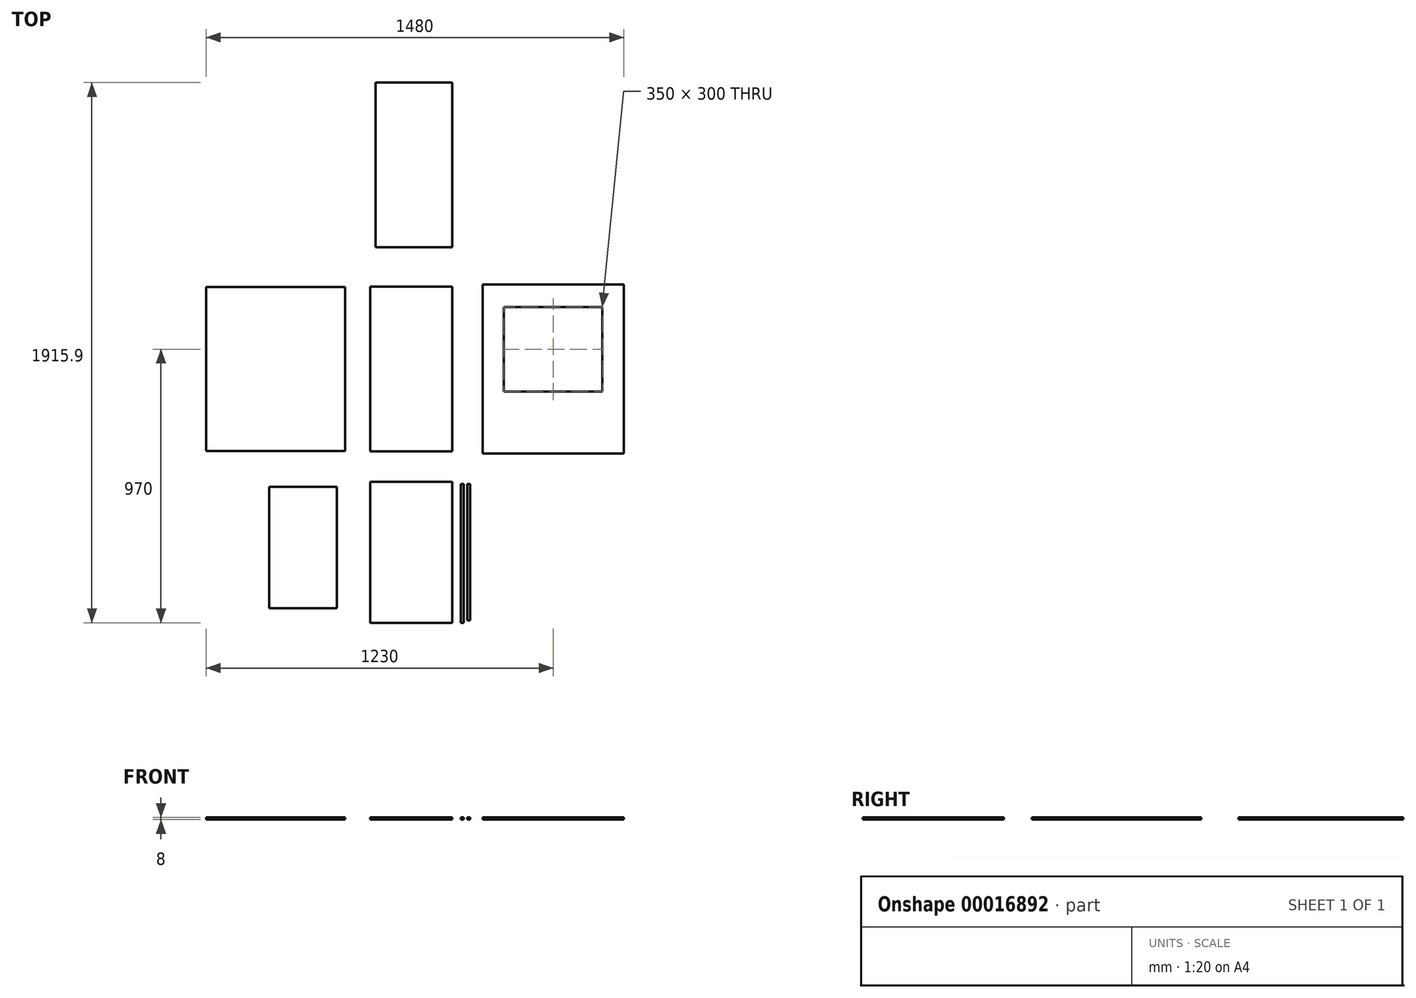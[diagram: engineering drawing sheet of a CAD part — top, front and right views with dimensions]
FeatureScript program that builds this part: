
annotation { "Feature Type Name" : "Feature", "Feature Type Description" : "" }
export const myFeature = defineFeature(function(context is Context, id is Id, definition is map)
    precondition{}
    {
        {
            var Q0;
            Q0=qCreatedBy(makeId("Top.planeOp"),FACE);
            var sketch = newSketch(context, id + "F0", { "sketchPlane" : qUnion([Q0])});
            skLineSegment(sketch, "E0.rect.bottom", {"start": v(140, 300) * mm, "end": v(-140, 300) * mm, "construction": true});
            skLineSegment(sketch, "E0.rect.top", {"start": v(140, -300) * mm, "end": v(-140, -300) * mm, "construction": true});
            skLineSegment(sketch, "E0.rect.left", {"start": v(140, 300) * mm, "end": v(140, -300) * mm, "construction": true});
            skLineSegment(sketch, "E0.rect.right", {"start": v(-140, 300) * mm, "end": v(-140, -300) * mm, "construction": true});
            skPoint(sketch, "E0.rect.middle", {"position": v(0, 0) * mm});
            skLineSegment(sketch, "E1.bottom", {"start": v(240, 300) * mm, "end": v(740, 300) * mm});
            skLineSegment(sketch, "E1.top", {"start": v(240, -300) * mm, "end": v(740, -300) * mm});
            skLineSegment(sketch, "E1.left", {"start": v(240, 300) * mm, "end": v(240, -300) * mm});
            skLineSegment(sketch, "E1.right", {"start": v(740, 300) * mm, "end": v(740, -300) * mm});
            skLineSegment(sketch, "E2.bottom", {"start": v(-240, 300) * mm, "end": v(-740, 300) * mm, "construction": true});
            skLineSegment(sketch, "E2.top", {"start": v(-240, -300) * mm, "end": v(-740, -300) * mm, "construction": true});
            skLineSegment(sketch, "E2.left", {"start": v(-240, 300) * mm, "end": v(-240, -300) * mm, "construction": true});
            skLineSegment(sketch, "E2.right", {"start": v(-740, 300) * mm, "end": v(-740, -300) * mm, "construction": true});
            skLineSegment(sketch, "E3.bottom", {"start": v(-140, -400) * mm, "end": v(140, -400) * mm, "construction": true});
            skLineSegment(sketch, "E3.top", {"start": v(-140, -900) * mm, "end": v(140, -900) * mm, "construction": true});
            skLineSegment(sketch, "E3.left", {"start": v(-140, -400) * mm, "end": v(-140, -900) * mm, "construction": true});
            skLineSegment(sketch, "E3.right", {"start": v(140, -400) * mm, "end": v(140, -900) * mm, "construction": true});
            skLineSegment(sketch, "E4", {"start": v(-740, 442.84) * mm, "end": v(-732, 442.84) * mm});
            skLineSegment(sketch, "E5", {"start": v(-240, 442.84) * mm, "end": v(-248, 442.84) * mm, "construction": true});
            skLineSegment(sketch, "E6", {"start": v(-732, 442.84) * mm, "end": v(-732, -300) * mm, "construction": true});
            skLineSegment(sketch, "E7", {"start": v(-248, 442.84) * mm, "end": v(-248, -300) * mm, "construction": true});
            skLineSegment(sketch, "E8", {"start": v(240, 442.84) * mm, "end": v(248, 442.84) * mm, "construction": true});
            skLineSegment(sketch, "E9", {"start": v(740, 442.84) * mm, "end": v(732, 442.84) * mm, "construction": true});
            skLineSegment(sketch, "E10", {"start": v(248, 442.84) * mm, "end": v(248, -300) * mm, "construction": true});
            skLineSegment(sketch, "E11", {"start": v(732, 442.84) * mm, "end": v(732, -300) * mm, "construction": true});
            skLineSegment(sketch, "E12", {"start": v(-192.24, -400) * mm, "end": v(-192.24, -408) * mm, "construction": true});
            skLineSegment(sketch, "E13", {"start": v(-140, -356.89) * mm, "end": v(-132, -356.89) * mm, "construction": true});
            skLineSegment(sketch, "E14", {"start": v(140, -941.5) * mm, "end": v(132, -941.5) * mm, "construction": true});
            skLineSegment(sketch, "E15", {"start": v(184.35, -900) * mm, "end": v(184.35, -892) * mm, "construction": true});
            skLineSegment(sketch, "E16", {"start": v(-132, -356.89) * mm, "end": v(-132, -900) * mm, "construction": true});
            skLineSegment(sketch, "E17", {"start": v(-192.24, -408) * mm, "end": v(140, -408) * mm, "construction": true});
            skLineSegment(sketch, "E18", {"start": v(132, -941.5) * mm, "end": v(132, -900) * mm, "construction": true});
            skLineSegment(sketch, "E19", {"start": v(184.35, -892) * mm, "end": v(-140, -892) * mm, "construction": true});
            skLineSegment(sketch, "E20.bottom", {"start": v(240, 300) * mm, "end": v(315, 300) * mm, "construction": true});
            skLineSegment(sketch, "E20.top", {"start": v(240, 220) * mm, "end": v(315, 220) * mm, "construction": true});
            skLineSegment(sketch, "E20.left", {"start": v(240, 300) * mm, "end": v(240, 220) * mm, "construction": true});
            skLineSegment(sketch, "E20.right", {"start": v(315, 300) * mm, "end": v(315, 220) * mm, "construction": true});
            skLineSegment(sketch, "E21.bottom", {"start": v(740, 300) * mm, "end": v(665, 300) * mm, "construction": true});
            skLineSegment(sketch, "E21.top", {"start": v(740, 220) * mm, "end": v(665, 220) * mm, "construction": true});
            skLineSegment(sketch, "E21.left", {"start": v(740, 300) * mm, "end": v(740, 220) * mm, "construction": true});
            skLineSegment(sketch, "E21.right", {"start": v(665, 300) * mm, "end": v(665, 220) * mm, "construction": true});
            skLineSegment(sketch, "E22.bottom", {"start": v(740, -300) * mm, "end": v(665, -300) * mm, "construction": true});
            skLineSegment(sketch, "E22.top", {"start": v(740, -80) * mm, "end": v(665, -80) * mm, "construction": true});
            skLineSegment(sketch, "E22.left", {"start": v(740, -300) * mm, "end": v(740, -80) * mm, "construction": true});
            skLineSegment(sketch, "E22.right", {"start": v(665, -300) * mm, "end": v(665, -80) * mm, "construction": true});
            skLineSegment(sketch, "E23.bottom", {"start": v(240, -300) * mm, "end": v(315, -300) * mm, "construction": true});
            skLineSegment(sketch, "E23.top", {"start": v(240, -80) * mm, "end": v(315, -80) * mm, "construction": true});
            skLineSegment(sketch, "E23.left", {"start": v(240, -300) * mm, "end": v(240, -80) * mm, "construction": true});
            skLineSegment(sketch, "E23.right", {"start": v(315, -300) * mm, "end": v(315, -80) * mm, "construction": true});
            skLineSegment(sketch, "E24.right", {"start": v(-732, 300) * mm, "end": v(-732, 292) * mm});
            skLineSegment(sketch, "E25.right", {"start": v(732, 300) * mm, "end": v(732, -300) * mm, "construction": true});
            skLineSegment(sketch, "E26.bottom", {"start": v(315, 220) * mm, "end": v(665, 220) * mm});
            skLineSegment(sketch, "E26.top", {"start": v(315, -80) * mm, "end": v(665, -80) * mm});
            skLineSegment(sketch, "E26.left", {"start": v(315, 220) * mm, "end": v(315, -80) * mm});
            skLineSegment(sketch, "E26.right", {"start": v(665, 220) * mm, "end": v(665, -80) * mm});
            skLineSegment(sketch, "E27", {"start": v(-132, -356.89) * mm, "end": v(-132, 300) * mm, "construction": true});
            skLineSegment(sketch, "E28", {"start": v(132, -400) * mm, "end": v(132, -292) * mm, "construction": true});
            skLineSegment(sketch, "E29", {"start": v(183.06, 300) * mm, "end": v(183.06, 292) * mm});
            skLineSegment(sketch, "E30", {"start": v(732, 292) * mm, "end": v(-740, 292) * mm, "construction": true});
            skLineSegment(sketch, "E31.bottom", {"start": v(-132, 292) * mm, "end": v(-122, 292) * mm, "construction": true});
            skLineSegment(sketch, "E31.top", {"start": v(-132, 282) * mm, "end": v(-122, 282) * mm, "construction": true});
            skLineSegment(sketch, "E31.left", {"start": v(-132, 292) * mm, "end": v(-132, 282) * mm, "construction": true});
            skLineSegment(sketch, "E31.right", {"start": v(-122, 292) * mm, "end": v(-122, 282) * mm, "construction": true});
            skLineSegment(sketch, "E32.bottom", {"start": v(132, 292) * mm, "end": v(122, 292) * mm, "construction": true});
            skLineSegment(sketch, "E32.top", {"start": v(132, 282) * mm, "end": v(122, 282) * mm, "construction": true});
            skLineSegment(sketch, "E32.left", {"start": v(132, 292) * mm, "end": v(132, 282) * mm, "construction": true});
            skLineSegment(sketch, "E32.right", {"start": v(122, 292) * mm, "end": v(122, 282) * mm, "construction": true});
            skLineSegment(sketch, "E33.left", {"start": v(-732, 292) * mm, "end": v(-732, 292) * mm});
            skLineSegment(sketch, "E34.bottom", {"start": v(-248, 292) * mm, "end": v(-258, 292) * mm, "construction": true});
            skLineSegment(sketch, "E34.left", {"start": v(-248, 292) * mm, "end": v(-248, 282) * mm, "construction": true});
            skLineSegment(sketch, "E35", {"start": v(-780.37, -300) * mm, "end": v(-780.37, -292) * mm, "construction": true});
            skLineSegment(sketch, "E36", {"start": v(-780.37, -292) * mm, "end": v(740, -292) * mm, "construction": true});
            skLineSegment(sketch, "E37.bottom", {"start": v(-732, -292) * mm, "end": v(-722, -292) * mm, "construction": true});
            skLineSegment(sketch, "E37.left", {"start": v(-732, -292) * mm, "end": v(-732, -282) * mm, "construction": true});
            skLineSegment(sketch, "E38.bottom", {"start": v(-248, -292) * mm, "end": v(-258, -292) * mm, "construction": true});
            skLineSegment(sketch, "E38.left", {"start": v(-248, -292) * mm, "end": v(-248, -282) * mm, "construction": true});
            skLineSegment(sketch, "E39.bottom", {"start": v(-132, -292) * mm, "end": v(-122, -292) * mm, "construction": true});
            skLineSegment(sketch, "E39.top", {"start": v(-132, -282) * mm, "end": v(-122, -282) * mm, "construction": true});
            skLineSegment(sketch, "E39.left", {"start": v(-132, -292) * mm, "end": v(-132, -282) * mm, "construction": true});
            skLineSegment(sketch, "E39.right", {"start": v(-122, -292) * mm, "end": v(-122, -282) * mm, "construction": true});
            skLineSegment(sketch, "E40.bottom", {"start": v(132, -292) * mm, "end": v(122, -292) * mm, "construction": true});
            skLineSegment(sketch, "E40.top", {"start": v(132, -282) * mm, "end": v(122, -282) * mm, "construction": true});
            skLineSegment(sketch, "E40.left", {"start": v(132, -292) * mm, "end": v(132, -282) * mm, "construction": true});
            skLineSegment(sketch, "E40.right", {"start": v(122, -292) * mm, "end": v(122, -282) * mm, "construction": true});
            skLineSegment(sketch, "E41.bottom", {"start": v(-132, -408) * mm, "end": v(-122, -408) * mm, "construction": true});
            skLineSegment(sketch, "E41.top", {"start": v(-132, -418) * mm, "end": v(-122, -418) * mm, "construction": true});
            skLineSegment(sketch, "E41.right", {"start": v(-122, -408) * mm, "end": v(-122, -418) * mm, "construction": true});
            skLineSegment(sketch, "E42.bottom", {"start": v(132, -408) * mm, "end": v(122, -408) * mm, "construction": true});
            skLineSegment(sketch, "E42.top", {"start": v(132, -418) * mm, "end": v(122, -418) * mm, "construction": true});
            skLineSegment(sketch, "E42.left", {"start": v(132, -408) * mm, "end": v(132, -418) * mm, "construction": true});
            skLineSegment(sketch, "E42.right", {"start": v(122, -408) * mm, "end": v(122, -418) * mm, "construction": true});
            skLineSegment(sketch, "E43.bottom", {"start": v(-132, -892) * mm, "end": v(-122, -892) * mm, "construction": true});
            skLineSegment(sketch, "E43.top", {"start": v(-132, -882) * mm, "end": v(-122, -882) * mm, "construction": true});
            skLineSegment(sketch, "E43.right", {"start": v(-122, -892) * mm, "end": v(-122, -882) * mm, "construction": true});
            skLineSegment(sketch, "E44.top", {"start": v(132, -882) * mm, "end": v(122, -882) * mm, "construction": true});
            skLineSegment(sketch, "E44.right", {"start": v(122, -892) * mm, "end": v(122, -882) * mm, "construction": true});
            skLineSegment(sketch, "E45.bottom", {"start": v(248, -292) * mm, "end": v(258, -292) * mm, "construction": true});
            skLineSegment(sketch, "E45.top", {"start": v(248, -282) * mm, "end": v(258, -282) * mm, "construction": true});
            skLineSegment(sketch, "E45.left", {"start": v(248, -292) * mm, "end": v(248, -282) * mm, "construction": true});
            skLineSegment(sketch, "E45.right", {"start": v(258, -292) * mm, "end": v(258, -282) * mm, "construction": true});
            skLineSegment(sketch, "E46.bottom", {"start": v(732, -292) * mm, "end": v(722, -292) * mm, "construction": true});
            skLineSegment(sketch, "E46.top", {"start": v(732, -282) * mm, "end": v(722, -282) * mm, "construction": true});
            skLineSegment(sketch, "E46.left", {"start": v(732, -292) * mm, "end": v(732, -282) * mm, "construction": true});
            skLineSegment(sketch, "E46.right", {"start": v(722, -292) * mm, "end": v(722, -282) * mm, "construction": true});
            skLineSegment(sketch, "E47.bottom", {"start": v(248, 292) * mm, "end": v(258, 292) * mm, "construction": true});
            skLineSegment(sketch, "E47.top", {"start": v(248, 282) * mm, "end": v(258, 282) * mm, "construction": true});
            skLineSegment(sketch, "E47.left", {"start": v(248, 292) * mm, "end": v(248, 282) * mm, "construction": true});
            skLineSegment(sketch, "E47.right", {"start": v(258, 292) * mm, "end": v(258, 282) * mm, "construction": true});
            skLineSegment(sketch, "E48.bottom", {"start": v(732, 292) * mm, "end": v(722, 292) * mm, "construction": true});
            skLineSegment(sketch, "E48.top", {"start": v(732, 282) * mm, "end": v(722, 282) * mm, "construction": true});
            skLineSegment(sketch, "E48.left", {"start": v(732, 292) * mm, "end": v(732, 282) * mm, "construction": true});
            skLineSegment(sketch, "E48.right", {"start": v(722, 292) * mm, "end": v(722, 282) * mm, "construction": true});
            skLineSegment(sketch, "E49", {"start": v(-732, 284) * mm, "end": v(-732, 282) * mm, "construction": true});
            skLineSegment(sketch, "E50", {"start": v(-732, 292) * mm, "end": v(-732, 284) * mm, "construction": true});
            skLineSegment(sketch, "E51.bottom", {"start": v(-122, -418) * mm, "end": v(122, -418) * mm, "construction": true});
            skLineSegment(sketch, "E51.top", {"start": v(-122, -882) * mm, "end": v(122, -882) * mm, "construction": true});
            skLineSegment(sketch, "E51.left", {"start": v(-122, -418) * mm, "end": v(-122, -882) * mm, "construction": true});
            skLineSegment(sketch, "E51.right", {"start": v(122, -418) * mm, "end": v(122, -882) * mm, "construction": true});
            skLineSegment(sketch, "E52.bottom", {"start": v(-276.09, -418) * mm, "end": v(-516.09, -418) * mm});
            skLineSegment(sketch, "E52.top", {"start": v(-276.09, -848) * mm, "end": v(-516.09, -848) * mm});
            skLineSegment(sketch, "E52.left", {"start": v(-276.09, -418) * mm, "end": v(-276.09, -848) * mm});
            skLineSegment(sketch, "E52.right", {"start": v(-516.09, -418) * mm, "end": v(-516.09, -848) * mm});
            skLineSegment(sketch, "E53.bottom", {"start": v(-140, 292) * mm, "end": v(140, 292) * mm});
            skLineSegment(sketch, "E53.top", {"start": v(-140, -292) * mm, "end": v(140, -292) * mm});
            skLineSegment(sketch, "E53.left", {"start": v(-140, 292) * mm, "end": v(-140, -292) * mm, "construction": true});
            skLineSegment(sketch, "E53.right", {"start": v(140, 292) * mm, "end": v(140, -292) * mm, "construction": true});
            skLineSegment(sketch, "E54.bottom", {"start": v(-140, 292) * mm, "end": v(-141, 292) * mm});
            skLineSegment(sketch, "E54.top", {"start": v(-140, -292) * mm, "end": v(-141, -292) * mm});
            skLineSegment(sketch, "E54.right", {"start": v(-141, 292) * mm, "end": v(-141, -292) * mm, "construction": true});
            skLineSegment(sketch, "E55.bottom", {"start": v(-141, 292) * mm, "end": v(-150, 292) * mm});
            skLineSegment(sketch, "E55.top", {"start": v(-141, -292) * mm, "end": v(-150, -292) * mm});
            skLineSegment(sketch, "E55.right", {"start": v(-150, 292) * mm, "end": v(-150, -292) * mm, "construction": true});
            skLineSegment(sketch, "E56.bottom", {"start": v(-150, -292) * mm, "end": v(-151, -292) * mm});
            skLineSegment(sketch, "E56.top", {"start": v(-150, 292) * mm, "end": v(-151, 292) * mm});
            skLineSegment(sketch, "E56.left", {"start": v(-150, -292) * mm, "end": v(-150, 292) * mm, "construction": true});
            skLineSegment(sketch, "E56.right", {"start": v(-151, -292) * mm, "end": v(-151, 292) * mm, "construction": true});
            skLineSegment(sketch, "E57.bottom", {"start": v(-151, 292) * mm, "end": v(-159, 292) * mm});
            skLineSegment(sketch, "E57.top", {"start": v(-151, -292) * mm, "end": v(-159, -292) * mm});
            skLineSegment(sketch, "E57.left", {"start": v(-151, 292) * mm, "end": v(-151, -292) * mm, "construction": true});
            skLineSegment(sketch, "E57.right", {"start": v(-159, 292) * mm, "end": v(-159, -292) * mm});
            skLineSegment(sketch, "E58", {"start": v(-159, -292) * mm, "end": v(-159, -941.14) * mm, "construction": true});
            skLineSegment(sketch, "E59", {"start": v(-159, -941.14) * mm, "end": v(-140, -941.14) * mm, "construction": true});
            skLineSegment(sketch, "E60", {"start": v(-140, -941.14) * mm, "end": v(-140, -900) * mm, "construction": true});
            skLineSegment(sketch, "E61", {"start": v(-140, -900) * mm, "end": v(-159, -900) * mm, "construction": true});
            skLineSegment(sketch, "E62", {"start": v(-140, -400) * mm, "end": v(-159, -400) * mm, "construction": true});
            skLineSegment(sketch, "E63.bottom", {"start": v(-159, -400) * mm, "end": v(140, -400) * mm});
            skLineSegment(sketch, "E63.top", {"start": v(-159, -900) * mm, "end": v(140, -900) * mm});
            skLineSegment(sketch, "E63.left", {"start": v(-159, -400) * mm, "end": v(-159, -900) * mm});
            skLineSegment(sketch, "E64.top", {"start": v(248, -292) * mm, "end": v(732, -292) * mm, "construction": true});
            skLineSegment(sketch, "E64.left", {"start": v(248, 300) * mm, "end": v(248, -292) * mm, "construction": true});
            skLineSegment(sketch, "E64.right", {"start": v(732, 300) * mm, "end": v(732, -292) * mm, "construction": true});
            skLineSegment(sketch, "E65.bottom", {"start": v(-140, 431.9) * mm, "end": v(132, 431.9) * mm});
            skLineSegment(sketch, "E65.top", {"start": v(-140, 1015.9) * mm, "end": v(132, 1015.9) * mm});
            skLineSegment(sketch, "E65.left", {"start": v(-140, 431.9) * mm, "end": v(-140, 1015.9) * mm, "construction": true});
            skLineSegment(sketch, "E65.right", {"start": v(132, 431.9) * mm, "end": v(132, 1015.9) * mm, "construction": true});
            skLineSegment(sketch, "E66", {"start": v(248, 292) * mm, "end": v(732, 292) * mm, "construction": true});
            skLineSegment(sketch, "E67.bottom", {"start": v(132, 431.9) * mm, "end": v(140, 431.9) * mm});
            skLineSegment(sketch, "E67.top", {"start": v(132, 1015.9) * mm, "end": v(140, 1015.9) * mm});
            skLineSegment(sketch, "E67.left", {"start": v(132, 431.9) * mm, "end": v(132, 1015.9) * mm});
            skLineSegment(sketch, "E67.right", {"start": v(140, 431.9) * mm, "end": v(140, 1015.9) * mm, "construction": true});
            skLineSegment(sketch, "E68.bottom", {"start": v(-140, 431.9) * mm, "end": v(-141, 431.9) * mm});
            skLineSegment(sketch, "E68.top", {"start": v(-140, 1015.9) * mm, "end": v(-141, 1015.9) * mm});
            skLineSegment(sketch, "E68.left", {"start": v(-140, 431.9) * mm, "end": v(-140, 1015.9) * mm});
            skLineSegment(sketch, "E68.right", {"start": v(-141, 431.9) * mm, "end": v(-141, 1015.9) * mm, "construction": true});
            skLineSegment(sketch, "E69.bottom", {"start": v(162.68, -408) * mm, "end": v(172.68, -408) * mm});
            skLineSegment(sketch, "E69.left", {"start": v(162.68, -408) * mm, "end": v(162.68, -882) * mm});
            skLineSegment(sketch, "E69.right", {"start": v(172.68, -408) * mm, "end": v(172.68, -882) * mm});
            skLineSegment(sketch, "E70", {"start": v(162.68, -882) * mm, "end": v(162.68, -892) * mm});
            skLineSegment(sketch, "E71", {"start": v(162.68, -892) * mm, "end": v(172.68, -892) * mm, "construction": true});
            skLineSegment(sketch, "E72", {"start": v(172.68, -892) * mm, "end": v(172.68, -882) * mm});
            skLineSegment(sketch, "E73.left", {"start": v(-732, 300) * mm, "end": v(-732, -292) * mm, "construction": true});
            skLineSegment(sketch, "E73.right", {"start": v(-248, 300) * mm, "end": v(-248, -292) * mm, "construction": true});
            skLineSegment(sketch, "E74.bottom", {"start": v(-248, -292) * mm, "end": v(-740, -292) * mm, "construction": true});
            skLineSegment(sketch, "E74.top", {"start": v(-248, 292) * mm, "end": v(-740, 292) * mm, "construction": true});
            skLineSegment(sketch, "E74.left", {"start": v(-248, -292) * mm, "end": v(-248, 292) * mm});
            skLineSegment(sketch, "E74.right", {"start": v(-740, -292) * mm, "end": v(-740, 292) * mm});
            skLineSegment(sketch, "E75.top", {"start": v(162.68, -900) * mm, "end": v(172.68, -900) * mm});
            skLineSegment(sketch, "E75.left", {"start": v(162.68, -892) * mm, "end": v(162.68, -900) * mm});
            skLineSegment(sketch, "E75.right", {"start": v(172.68, -892) * mm, "end": v(172.68, -900) * mm});
            skLineSegment(sketch, "E76.bottom", {"start": v(185.79, -408) * mm, "end": v(195.79, -408) * mm});
            skLineSegment(sketch, "E76.top", {"start": v(185.79, -892) * mm, "end": v(195.79, -892) * mm});
            skLineSegment(sketch, "E76.left", {"start": v(185.79, -408) * mm, "end": v(185.79, -892) * mm});
            skLineSegment(sketch, "E76.right", {"start": v(195.79, -408) * mm, "end": v(195.79, -892) * mm});
            skLineSegment(sketch, "E77.0", {"start": v(-248, 290.5) * mm, "end": v(-740, 290.5) * mm});
            skLineSegment(sketch, "E78.0", {"start": v(-248, -290.5) * mm, "end": v(-740, -290.5) * mm});
            skLineSegment(sketch, "E79", {"start": v(132, -900) * mm, "end": v(132, -400) * mm});
            skLineSegment(sketch, "E80", {"start": v(132, -292) * mm, "end": v(132, 292) * mm});
            skLineSegment(sketch, "E81", {"start": v(132, 292) * mm, "end": v(132, 300) * mm, "construction": true});
            skSolve(sketch);
        }
        {
            var Q0;
            Q0=makeQuery(id+"F0.imprint","IMPRINT",FACE,{"disambiguationData":[TD([[makeQuery(id+"F0.imprint","IMPRINT",EDGE,{"derivedFrom":sQuery(id+"F0.wireOp",EDGE,"E65.bottom")}),1.0]])]});
            var Q1;
            Q1=makeQuery(id+"F0.imprint","IMPRINT",FACE,{"disambiguationData":[TD([[makeQuery(id+"F0.imprint","IMPRINT",EDGE,{"derivedFrom":sQuery(id+"F0.wireOp",EDGE,"E26.bottom")}),1.0]])]});
            var Q2;
            Q2=makeQuery(id+"F0.imprint","IMPRINT",FACE,{"disambiguationData":[TD([[makeQuery(id+"F0.imprint","IMPRINT",EDGE,{"derivedFrom":sQuery(id+"F0.wireOp",EDGE,"E53.bottom")}),-1.0]])]});
            var Q3;
            Q3=makeQuery(id+"F0.imprint","IMPRINT",FACE,{"disambiguationData":[TD([[makeQuery(id+"F0.imprint","IMPRINT",EDGE,{"derivedFrom":sQuery(id+"F0.wireOp",EDGE,"E63.bottom")}),-1.0]])]});
            var Q4;
            Q4=makeQuery(id+"F0.imprint","IMPRINT",FACE,{"disambiguationData":[TD([[makeQuery(id+"F0.imprint","IMPRINT",EDGE,{"derivedFrom":sQuery(id+"F0.wireOp",EDGE,"E52.bottom")}),1.0]])]});
            var Q5;
            Q5=makeQuery(id+"F0.imprint","IMPRINT",FACE,{"disambiguationData":[TD([[makeQuery(id+"F0.imprint","IMPRINT",EDGE,{"derivedFrom":sQuery(id+"F0.wireOp",EDGE,"E24.bottom")}),1.0]])]});
            var Q6;
            {var subQ0=sQuery(id+"F0.wireOp",EDGE,"be893e06-8e3d-42c5-8dc1-4e727d6ec9451");Q6=makeQuery(id+"F0.imprint","IMPRINT",FACE,{"disambiguationData":[TD([[makeQuery(id+"F0.imprint","IMPRINT",EDGE,{"derivedFrom":subQ0}),1.0]])]});}
            var Q7;
            Q7=makeQuery(id+"F0.imprint","IMPRINT",FACE,{"disambiguationData":[TD([[makeQuery(id+"F0.imprint","IMPRINT",EDGE,{"derivedFrom":sQuery(id+"F0.wireOp",EDGE,"bed136b5-45e1-4f38-b305-68be42ccbf5f")}),-1.0]])]});
            var Q8;
            {var subQ0=sQuery(id+"F0.wireOp",EDGE,"d1084443-12bb-47f2-b1df-bd5794965ff91");Q8=makeQuery(id+"F0.imprint","IMPRINT",FACE,{"disambiguationData":[TD([[makeQuery(id+"F0.imprint","IMPRINT",EDGE,{"derivedFrom":subQ0}),-1.0]])]});}
            var Q9;
            {var subQ1=sQuery(id+"F0.wireOp",EDGE,"d1084443-12bb-47f2-b1df-bd5794965ff91");Q9=makeQuery(id+"F0.imprint","IMPRINT",FACE,{"disambiguationData":[TD([[makeQuery(id+"F0.imprint","IMPRINT",EDGE,{"derivedFrom":subQ1}),1.0]])]});}
            var Q10;
            {var subQ1=sQuery(id+"F0.wireOp",EDGE,"72141153-4939-4217-9fa9-9b0f28127721.rect.left");Q10=makeQuery(id+"F0.imprint","IMPRINT",FACE,{"disambiguationData":[TD([[makeQuery(id+"F0.imprint","IMPRINT",EDGE,{"derivedFrom":subQ1}),-1.0]])]});}
            var Q11;
            Q11=makeQuery(id+"F0.imprint","IMPRINT",FACE,{"disambiguationData":[TD([[makeQuery(id+"F0.imprint","IMPRINT",EDGE,{"derivedFrom":sQuery(id+"F0.wireOp",EDGE,"E69.bottom")}),-1.0]])]});
            var Q12;
            Q12=makeQuery(id+"F0.imprint","IMPRINT",FACE,{"disambiguationData":[TD([[makeQuery(id+"F0.imprint","IMPRINT",EDGE,{"derivedFrom":sQuery(id+"F0.wireOp",EDGE,"d61294ae-2d91-410d-aaf6-2dedefb16167.bottom")}),1.0]])]});
            var Q13;
            {var subQ1=sQuery(id+"F0.wireOp",EDGE,"84a1b1db-46c9-4314-98f2-df0ab25bd294.0");Q13=makeQuery(id+"F0.imprint","IMPRINT",FACE,{"disambiguationData":[TD([[makeQuery(id+"F0.imprint","IMPRINT",EDGE,{"derivedFrom":subQ1}),1.0]])]});}
            var Q14;
            Q14=makeQuery(id+"F0.imprint","IMPRINT",FACE,{"disambiguationData":[TD([[makeQuery(id+"F0.imprint","IMPRINT",EDGE,{"derivedFrom":sQuery(id+"F0.wireOp",EDGE,"E74.bottom")}),-1.0]])]});
            var Q15;
            Q15=makeQuery(id+"F0.imprint","IMPRINT",FACE,{"disambiguationData":[TD([[makeQuery(id+"F0.imprint","IMPRINT",EDGE,{"derivedFrom":sQuery(id+"F0.wireOp",EDGE,"E76.bottom")}),-1.0]])]});
            var Q16;
            {var subQ2=sQuery(id+"F0.wireOp",EDGE,"E77.0");Q16=makeQuery(id+"F0.imprint","IMPRINT",FACE,{"disambiguationData":[TD([[makeQuery(id+"F0.imprint","IMPRINT",EDGE,{"derivedFrom":subQ2}),1.0]])]});}
            extrude(context, id + "F1", {"entities" : qUnion([Q0, Q1, Q2, Q3, Q4, Q5, Q6, Q7, Q8, Q9, Q10, Q11, Q12, Q13, Q14, Q15, Q16]), "depth" : 8 * mm});
        }
    });
